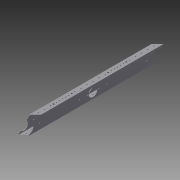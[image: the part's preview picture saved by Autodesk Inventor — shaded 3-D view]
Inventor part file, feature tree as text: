
AUTODESK INVENTOR PART (.ipt)
format: ipt  version: 2015 SP1 (Build 190203100, 203)  size: 302,080 bytes
history: native  units: in
note: dims shown in document units (in); Inventor stores cm internally (conversion verified against a paired STEP export)
features: sketch x8, projected_geometry x7, hole x5, extrude x3, pattern_linear x1
ambient origin geometry x8: Origin, YZ Plane, XZ Plane, XY Plane, X Axis, Y Axis, Z Axis, Center Point
bodies: Solid1 (feature_tree)
feature tree (24):
  extrude  "Extrusion1"  Depth=2.0in
  hole  "Hole1"  [1 undecoded]
  pattern_linear  "Rectangular Pattern1"  Count1=26 Spacing1=1.0in
  hole  "Hole2"  [1 undecoded]
  hole  "Hole3"  [1 undecoded]
  hole  "Hole4"  [1 undecoded]
  extrude  "Extrusion2"  Depth=1.0in
  hole  "Hole5"  [1 undecoded]
  extrude  "Extrusion3"  Depth=2.0in
  sketch  "Sketch1"  dims[d0=1.0in d1=2.0in]
  sketch  "Sketch2"  dims[d2=1.8in d3=0.8in]
  projected_geometry  "Projected Loop1"
  sketch  "Sketch3"  dims[d4=0.1in]
  projected_geometry  "Projected Loop2"
  sketch  "Sketch4"  dims[d5=0.1in]
  projected_geometry  "Projected Loop3"
  sketch  "Sketch5"  dims[d6=26.0in d7=0.0in]
  projected_geometry  "Projected Loop4"
  sketch  "Sketch6"  dims[d8=0.5in]
  projected_geometry  "Projected Loop5"
  sketch  "Sketch7"  dims[d9=0.5in]
  projected_geometry  "Projected Loop6"
  sketch  "Sketch8"  dims[d10=0.1562in d11=0.75in d12=0.375in d13=0.25in d14=0.5635in d15=1.0in d16=0.8108in d17=10.2362in d19=1.0in d20=2.5in d21=1.0in d22=2.5in d23=1.0in d24=1.0in d25=13.0in d26=1.5in d27=0.75in d28=0.375in d29=0.25in d30=0.5635in d31=1.0in d32=0.8108in d33=2.25in d34=2.25in d35=1.0in d36=1.0in d37=1.0in d38=1.0in d39=0.9375in d40=0.9375in d41=0.19in d42=0.75in d43=0.375in d44=0.25in d45=0.5635in d46=1.0in d47=0.8108in d48=1.0in d49=1.0in d50=4.1562in d51=4.1562in d52=0.19in d53=0.75in d54=0.375in d55=0.25in d56=0.5635in d57=1.0in d58=0.8108in d59=0.25in d60=0.25in d61=1.0in d62=0.5in d63=0.25in d64=1.0in d65=0.5in d66=0.25in d67=2.0in d68=0.0in d69=7.0in d70=8.0in d71=9.0in d72=10.0in d73=0.5in d74=0.5in d75=0.5in d76=0.5in d77=0.5in d78=0.5in d79=0.5in d80=0.5in d81=7.0in d82=8.0in d83=9.0in d84=10.0in d85=0.1562in d86=0.75in d87=0.375in d88=0.25in d89=0.5635in d90=1.0in d91=0.8108in d92=0.25in d93=0.25in d94=0.25in d95=0.25in d96=2.0in d97=0.0in]
  projected_geometry  "Projected Loop7"
note: 5 required parameter values undecoded (feature->parameter linkage not recoverable at this tier; creation-order binding heuristic only, values carry confidence <= 0.55)
